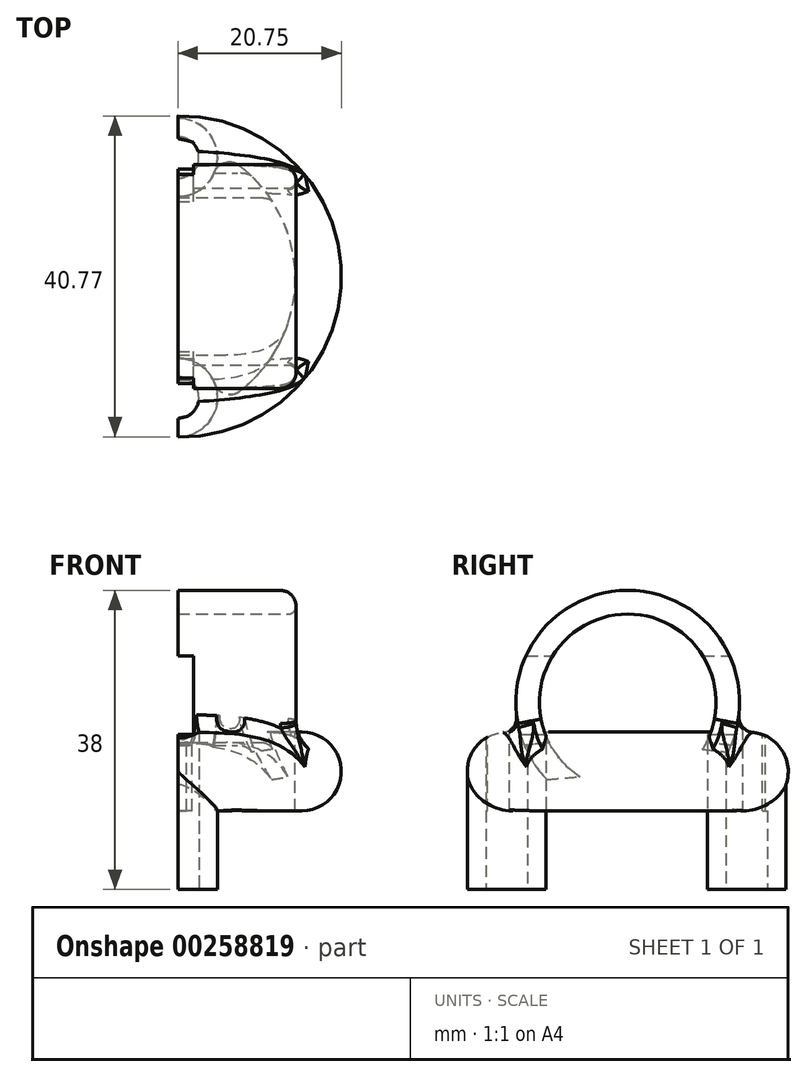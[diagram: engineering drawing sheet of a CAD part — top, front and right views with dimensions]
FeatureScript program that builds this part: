
annotation { "Feature Type Name" : "Feature", "Feature Type Description" : "" }
export const myFeature = defineFeature(function(context is Context, id is Id, definition is map)
    precondition{}
    {
        {
            var Q0;
            Q0=qCreatedBy(makeId("Top.planeOp"),FACE);
            var sketch = newSketch(context, id + "F0", { "sketchPlane" : qUnion([Q0])});
            skArc(sketch, "E0", {"start": v(0, 12.6) * mm, "mid": v(2.65, 15.25) * mm, "end": v(0, 17.9) * mm});
            skArc(sketch, "E1", {"start": v(0, -17.9) * mm, "mid": v(2.65, -15.25) * mm, "end": v(0, -12.6) * mm});
            skArc(sketch, "E2", {"start": v(0, 10.25) * mm, "mid": v(5, 15.25) * mm, "end": v(0, 20.25) * mm});
            skArc(sketch, "E3", {"start": v(0, -20.25) * mm, "mid": v(5, -15.25) * mm, "end": v(0, -10.25) * mm});
            skPoint(sketch, "E4.orphan", {"position": v(0, -21.4) * mm});
            skLineSegment(sketch, "E5", {"start": v(0, 10.25) * mm, "end": v(0, 12.6) * mm});
            skPoint(sketch, "E6.orphan", {"position": v(0, 6.06) * mm});
            skLineSegment(sketch, "E7.trimOffspring", {"start": v(0, 17.9) * mm, "end": v(0, 20.25) * mm});
            skLineSegment(sketch, "E8", {"start": v(0, -20.25) * mm, "end": v(0, -15.25) * mm});
            skPoint(sketch, "E9.right.end.orphan", {"position": v(-2, -20.25) * mm});
            skPoint(sketch, "E10.right.end.orphan", {"position": v(-2, -12.6) * mm});
            skLineSegment(sketch, "E11.trimOffspring", {"start": v(0, -12.6) * mm, "end": v(0, -10.25) * mm});
            skSolve(sketch);
        }
        {
            var Q0;
            Q0 = qSketchRegion(id + "F0", true);
            extrude(context, id + "F1", {"entities" : qUnion([Q0]), "depth" : 20 * mm});
        }
        {
            var Q0;
            Q0=makeQuery(id+"F1.opExtrude","CAP_FACE",FACE,{"disambiguationData":[OSD([sQuery(id+"F0.wireOp",EDGE,"E1"),sQuery(id+"F0.wireOp",EDGE,"E3"),sQuery(id+"F0.wireOp",EDGE,"E10.bottom"),sQuery(id+"F0.wireOp",EDGE,"E10.top"),sQuery(id+"F0.wireOp",EDGE,"E10.right"),sQuery(id+"F0.wireOp",EDGE,"E9.bottom"),sQuery(id+"F0.wireOp",EDGE,"E9.top"),sQuery(id+"F0.wireOp",EDGE,"E9.right")])],"isStart":false});
            var sketch = newSketch(context, id + "F2", { "sketchPlane" : qUnion([Q0])});
            skArc(sketch, "E12", {"start": v(0, -20.25) * mm, "mid": v(20.75, 0.14) * mm, "end": v(0, 20.52) * mm});
            skArc(sketch, "E13", {"start": v(0, -17.9) * mm, "mid": v(14.9, -0.13) * mm, "end": v(0, 17.63) * mm});
            skLineSegment(sketch, "E14", {"start": v(0, 17.63) * mm, "end": v(0, 20.52) * mm});
            skLineSegment(sketch, "E15", {"start": v(0, -20.25) * mm, "end": v(0, -17.9) * mm});
            skSolve(sketch);
        }
        {
            var Q0;
            Q0 = qSketchRegion(id + "F2", true);
            extrude(context, id + "F3", {"entities" : qUnion([Q0]), "operationType" : NewBodyOperationType.ADD, "oppositeDirection" : true, "depth" : 10 * mm});
        }
        {
            var Q0;
            Q0=makeQuery(id+"F1.opExtrude","SWEPT_FACE",FACE,{"disambiguationData":[OSD([sQuery(id+"F0.wireOp",EDGE,"E5")])]});
            cPlane(context, id + "F4", {"entities" : qUnion([Q0]), "cplaneType" : CPlaneType.OFFSET, "offset" : 5 * mm, "oppositeDirection" : true, "width" : 150 * mm, "height" : 150 * mm});
        }
        {
            var Q0;
            Q0=qCreatedBy(makeId("Right.planeOp"),FACE);
            cPlane(context, id + "F5", {"entities" : qUnion([Q0]), "cplaneType" : CPlaneType.OFFSET, "offset" : 15 * mm, "width" : 150 * mm, "height" : 150 * mm});
        }
        {
            var Q0;
            Q0=qCreatedBy(id+"F5.planeOp",FACE);
            var sketch = newSketch(context, id + "F6", { "sketchPlane" : qUnion([Q0])});
            skLineSegment(sketch, "E16", {"start": v(-14.8, 18.7) * mm, "end": v(15.62, 18.7) * mm, "construction": true});
            skArc(sketch, "E17", {"start": v(10.13, 18.7) * mm, "mid": v(0.13, 35) * mm, "end": v(-9.87, 18.7) * mm});
            skArc(sketch, "E18.0", {"start": v(13.26, 18.3) * mm, "mid": v(0.13, 38) * mm, "end": v(-13, 18.3) * mm});
            skLineSegment(sketch, "E19", {"start": v(10.13, 18.7) * mm, "end": v(13.26, 18.3) * mm});
            skLineSegment(sketch, "E20", {"start": v(-13, 18.3) * mm, "end": v(-9.87, 18.7) * mm});
            skSolve(sketch);
        }
        {
            var Q0;
            Q0=makeQuery(id+"F6.imprint","IMPRINT",FACE,{"disambiguationData":[TD([[makeQuery(id+"F6.imprint","IMPRINT",EDGE,{"derivedFrom":sQuery(id+"F6.wireOp",EDGE,"E17")}),-1.0]])]});
            var Q1;
            Q1=makeQuery(id+"F1.opExtrude","SWEPT_FACE",FACE,{"disambiguationData":[OSD([sQuery(id+"F0.wireOp",EDGE,"E11.trimOffspring")])]});
            extrude(context, id + "F7", {"entities" : qUnion([Q0]), "operationType" : NewBodyOperationType.ADD, "endBound" : BoundingType.UP_TO_SURFACE, "oppositeDirection" : true, "endBoundEntityFace" : qUnion([Q1]), "depth" : 15 * mm});
        }
        {
            var Q0;
            {var subQ1=sQuery(id+"F0.wireOp",EDGE,"E2");var subQ4=sQuery(id+"F2.wireOp",EDGE,"E13");Q0=makeQuery(id+"F7.boolean.opBoolean","INTERSECT",EDGE,{"derivedFrom":[makeQuery(id+"F3.boolean.opBoolean","SPLIT",FACE,{"disambiguationData":[TD([makeQuery(id+"F1.opExtrude","SWEPT_FACE",FACE,{"disambiguationData":[OSD([subQ1])]})])],"derivedFrom":makeQuery(id+"F3.opExtrude","SWEPT_FACE",FACE,{"disambiguationData":[OSD([subQ4])]})}),makeQuery(id+"F7.opExtrude","SWEPT_FACE",FACE,{"disambiguationData":[OSD([sQuery(id+"F6.wireOp",EDGE,"E19")])]})]});}
            fillet(context, id + "F8", {"entities" : qUnion([Q0]), "radius" : 1 * mm, "tangentPropagation" : true, "allowEdgeOverflow" : false});
        }
        {
            var Q0;
            {var subQ1=sQuery(id+"F0.wireOp",EDGE,"E2");var subQ4=sQuery(id+"F2.wireOp",EDGE,"E13");Q0=makeQuery(id+"F7.boolean.opBoolean","INTERSECT",EDGE,{"derivedFrom":[makeQuery(id+"F3.boolean.opBoolean","SPLIT",FACE,{"disambiguationData":[TD([makeQuery(id+"F1.opExtrude","SWEPT_FACE",FACE,{"disambiguationData":[OSD([subQ1])]})])],"derivedFrom":makeQuery(id+"F3.opExtrude","SWEPT_FACE",FACE,{"disambiguationData":[OSD([subQ4])]})}),makeQuery(id+"F7.opExtrude","SWEPT_FACE",FACE,{"disambiguationData":[OSD([sQuery(id+"F6.wireOp",EDGE,"E20")])]})]});}
            fillet(context, id + "F9", {"entities" : qUnion([Q0]), "radius" : 5 * mm, "tangentPropagation" : true, "allowEdgeOverflow" : false});
        }
        {
            var Q0;
            Q0=makeQuery(id+"F3.opExtrude","CAP_EDGE",EDGE,{"disambiguationData":[OSD([sQuery(id+"F2.wireOp",EDGE,"E12")])],"isStart":true});
            var Q1;
            Q1=makeQuery(id+"F3.opExtrude","CAP_EDGE",EDGE,{"disambiguationData":[OSD([sQuery(id+"F2.wireOp",EDGE,"E12")])],"isStart":false});
            fillet(context, id + "F10", {"entities" : qUnion([Q0, Q1]), "radius" : 5 * mm, "tangentPropagation" : true, "allowEdgeOverflow" : false});
        }
        {
            var Q0;
            Q0=makeQuery(id+"F10.opFillet","BLEND_EDGE",EDGE,{"disambiguationData":[OD(1.0)],"blendedFrom":[makeQuery(id+"F3.opExtrude","CAP_EDGE",EDGE,{"disambiguationData":[OSD([sQuery(id+"F2.wireOp",EDGE,"E12")])],"isStart":true}),makeQuery(id+"F7.opExtrude","CAP_FACE",FACE,{"disambiguationData":[OSD([sQuery(id+"F6.wireOp",EDGE,"E17"),sQuery(id+"F6.wireOp",EDGE,"E18.0"),sQuery(id+"F6.wireOp",EDGE,"E19"),sQuery(id+"F6.wireOp",EDGE,"E20")])],"isStart":true})],"blendedInto":[makeQuery(id+"F7.opExtrude","CAP_FACE",FACE,{"disambiguationData":[OSD([sQuery(id+"F6.wireOp",EDGE,"E17"),sQuery(id+"F6.wireOp",EDGE,"E18.0"),sQuery(id+"F6.wireOp",EDGE,"E19"),sQuery(id+"F6.wireOp",EDGE,"E20")])],"isStart":true})]});
            var Q1;
            Q1=makeQuery(id+"F10.opFillet","BLEND_EDGE",EDGE,{"disambiguationData":[OD(0.0)],"blendedFrom":[makeQuery(id+"F3.opExtrude","CAP_EDGE",EDGE,{"disambiguationData":[OSD([sQuery(id+"F2.wireOp",EDGE,"E12")])],"isStart":true}),makeQuery(id+"F7.opExtrude","CAP_FACE",FACE,{"disambiguationData":[OSD([sQuery(id+"F6.wireOp",EDGE,"E17"),sQuery(id+"F6.wireOp",EDGE,"E18.0"),sQuery(id+"F6.wireOp",EDGE,"E19"),sQuery(id+"F6.wireOp",EDGE,"E20")])],"isStart":true})],"blendedInto":[makeQuery(id+"F7.opExtrude","CAP_FACE",FACE,{"disambiguationData":[OSD([sQuery(id+"F6.wireOp",EDGE,"E17"),sQuery(id+"F6.wireOp",EDGE,"E18.0"),sQuery(id+"F6.wireOp",EDGE,"E19"),sQuery(id+"F6.wireOp",EDGE,"E20")])],"isStart":true})]});
            fillet(context, id + "F11", {"entities" : qUnion([Q0, Q1]), "radius" : 5 * mm, "tangentPropagation" : true, "allowEdgeOverflow" : false});
        }
        {
            var Q0;
            Q0=makeQuery(id+"F7.opExtrude","CAP_EDGE",EDGE,{"disambiguationData":[OSD([sQuery(id+"F6.wireOp",EDGE,"E17")])],"isStart":true});
            fillet(context, id + "F12", {"entities" : qUnion([Q0]), "radius" : 1 * mm, "tangentPropagation" : true, "allowEdgeOverflow" : false});
        }
        {
            var Q0;
            Q0=makeQuery(id+"F10.opFillet","BLEND_EDGE",EDGE,{"disambiguationData":[OD(1.0)],"blendedFrom":[makeQuery(id+"F3.opExtrude","CAP_EDGE",EDGE,{"disambiguationData":[OSD([sQuery(id+"F2.wireOp",EDGE,"E12")])],"isStart":true}),makeQuery(id+"F7.opExtrude","SWEPT_FACE",FACE,{"disambiguationData":[OSD([sQuery(id+"F6.wireOp",EDGE,"E18.0")])]})],"blendedInto":[makeQuery(id+"F7.opExtrude","SWEPT_FACE",FACE,{"disambiguationData":[OSD([sQuery(id+"F6.wireOp",EDGE,"E18.0")])]})]});
            var Q1;
            Q1=makeQuery(id+"F10.opFillet","BLEND_EDGE",EDGE,{"disambiguationData":[OD(0.0)],"blendedFrom":[makeQuery(id+"F3.opExtrude","CAP_EDGE",EDGE,{"disambiguationData":[OSD([sQuery(id+"F2.wireOp",EDGE,"E12")])],"isStart":true}),makeQuery(id+"F7.opExtrude","SWEPT_FACE",FACE,{"disambiguationData":[OSD([sQuery(id+"F6.wireOp",EDGE,"E18.0")])]})],"blendedInto":[makeQuery(id+"F7.opExtrude","SWEPT_FACE",FACE,{"disambiguationData":[OSD([sQuery(id+"F6.wireOp",EDGE,"E18.0")])]})]});
            fillet(context, id + "F13", {"entities" : qUnion([Q0, Q1]), "radius" : 2 * mm, "tangentPropagation" : true, "allowEdgeOverflow" : false});
        }
        {
            var Q0;
            Q0=makeQuery(id+"F7.opExtrude","CAP_EDGE",EDGE,{"disambiguationData":[OSD([sQuery(id+"F6.wireOp",EDGE,"E18.0")])],"isStart":true});
            fillet(context, id + "F14", {"entities" : qUnion([Q0]), "radius" : 2 * mm, "tangentPropagation" : true, "allowEdgeOverflow" : false});
        }
        {
            var Q0;
            {var subQ0=sQuery(id+"F0.wireOp",EDGE,"E11.trimOffspring");Q0=makeQuery(id+"F7.boolean.opBoolean","MERGE",FACE,{"derivedFrom":[makeQuery(id+"F1.opExtrude","SWEPT_FACE",FACE,{"disambiguationData":[OSD([sQuery(id+"F0.wireOp",EDGE,"E5")])]}),makeQuery(id+"F1.opExtrude","SWEPT_FACE",FACE,{"disambiguationData":[OSD([subQ0])]}),makeQuery(id+"F7.opExtrude","CAP_FACE",FACE,{"disambiguationData":[OSD([subQ0])],"isStart":false})]});}
            var sketch = newSketch(context, id + "F15", { "sketchPlane" : qUnion([Q0])});
            skLineSegment(sketch, "E21.bottom", {"start": v(10.43, 19.69) * mm, "end": v(-23.94, 19.69) * mm});
            skLineSegment(sketch, "E21.top", {"start": v(16, 29.69) * mm, "end": v(-23.94, 29.69) * mm});
            skLineSegment(sketch, "E21.left", {"start": v(16, 19.69) * mm, "end": v(16, 29.69) * mm});
            skLineSegment(sketch, "E21.right", {"start": v(-23.94, 19.69) * mm, "end": v(-23.94, 29.69) * mm});
            skLineSegment(sketch, "E22", {"start": v(10.43, 19.69) * mm, "end": v(16, 19.69) * mm});
            skSolve(sketch);
        }
        {
            var Q0;
            Q0 = qSketchRegion(id + "F15", true);
            extrude(context, id + "F16", {"entities" : qUnion([Q0]), "operationType" : NewBodyOperationType.REMOVE, "oppositeDirection" : true, "depth" : 2 * mm});
        }
        {
            var Q0;
            Q0=makeQuery(id+"F7.boolean.opBoolean","INTERSECT",EDGE,{"disambiguationData":[OD(1.0)],"derivedFrom":[makeQuery(id+"F3.boolean.opBoolean","MERGE",FACE,{"derivedFrom":[makeQuery(id+"F1.opExtrude","CAP_FACE",FACE,{"disambiguationData":[OSD([sQuery(id+"F0.wireOp",EDGE,"E0"),sQuery(id+"F0.wireOp",EDGE,"E2"),sQuery(id+"F0.wireOp",EDGE,"E5"),sQuery(id+"F0.wireOp",EDGE,"E7.trimOffspring")])],"isStart":false}),makeQuery(id+"F1.opExtrude","CAP_FACE",FACE,{"disambiguationData":[OSD([sQuery(id+"F0.wireOp",EDGE,"E1"),sQuery(id+"F0.wireOp",EDGE,"E3"),sQuery(id+"F0.wireOp",EDGE,"E8"),sQuery(id+"F0.wireOp",EDGE,"E11.trimOffspring")])],"isStart":false}),makeQuery(id+"F3.opExtrude","CAP_FACE",FACE,{"disambiguationData":[OSD([sQuery(id+"F2.wireOp",EDGE,"E12"),sQuery(id+"F2.wireOp",EDGE,"E13"),sQuery(id+"F2.wireOp",EDGE,"E14"),sQuery(id+"F2.wireOp",EDGE,"E15")])],"isStart":true})]}),makeQuery(id+"F7.opExtrude","SWEPT_FACE",FACE,{"disambiguationData":[OSD([sQuery(id+"F6.wireOp",EDGE,"E18.0")])]})]});
            var Q1;
            Q1=makeQuery(id+"F7.boolean.opBoolean","INTERSECT",EDGE,{"disambiguationData":[OD(0.0)],"derivedFrom":[makeQuery(id+"F3.boolean.opBoolean","MERGE",FACE,{"derivedFrom":[makeQuery(id+"F1.opExtrude","CAP_FACE",FACE,{"disambiguationData":[OSD([sQuery(id+"F0.wireOp",EDGE,"E0"),sQuery(id+"F0.wireOp",EDGE,"E2"),sQuery(id+"F0.wireOp",EDGE,"E5"),sQuery(id+"F0.wireOp",EDGE,"E7.trimOffspring")])],"isStart":false}),makeQuery(id+"F1.opExtrude","CAP_FACE",FACE,{"disambiguationData":[OSD([sQuery(id+"F0.wireOp",EDGE,"E1"),sQuery(id+"F0.wireOp",EDGE,"E3"),sQuery(id+"F0.wireOp",EDGE,"E8"),sQuery(id+"F0.wireOp",EDGE,"E11.trimOffspring")])],"isStart":false}),makeQuery(id+"F3.opExtrude","CAP_FACE",FACE,{"disambiguationData":[OSD([sQuery(id+"F2.wireOp",EDGE,"E12"),sQuery(id+"F2.wireOp",EDGE,"E13"),sQuery(id+"F2.wireOp",EDGE,"E14"),sQuery(id+"F2.wireOp",EDGE,"E15")])],"isStart":true})]}),makeQuery(id+"F7.opExtrude","SWEPT_FACE",FACE,{"disambiguationData":[OSD([sQuery(id+"F6.wireOp",EDGE,"E18.0")])]})]});
            fillet(context, id + "F17", {"entities" : qUnion([Q0, Q1]), "radius" : 2 * mm, "tangentPropagation" : true, "allowEdgeOverflow" : false});
        }
        {
            var Q0;
            Q0=makeQuery(id+"F3.boolean.opBoolean","INTERSECT",EDGE,{"derivedFrom":[makeQuery(id+"F1.opExtrude","SWEPT_FACE",FACE,{"disambiguationData":[OSD([sQuery(id+"F0.wireOp",EDGE,"E3")])]}),makeQuery(id+"F3.opExtrude","SWEPT_FACE",FACE,{"disambiguationData":[OSD([sQuery(id+"F2.wireOp",EDGE,"E13")])]})]});
            var Q1;
            Q1=makeQuery(id+"F3.boolean.opBoolean","INTERSECT",EDGE,{"derivedFrom":[makeQuery(id+"F1.opExtrude","SWEPT_FACE",FACE,{"disambiguationData":[OSD([sQuery(id+"F0.wireOp",EDGE,"E2")])]}),makeQuery(id+"F3.opExtrude","SWEPT_FACE",FACE,{"disambiguationData":[OSD([sQuery(id+"F2.wireOp",EDGE,"E13")])]})]});
            fillet(context, id + "F18", {"entities" : qUnion([Q0, Q1]), "radius" : 2 * mm, "tangentPropagation" : true, "allowEdgeOverflow" : false});
        }
    });
